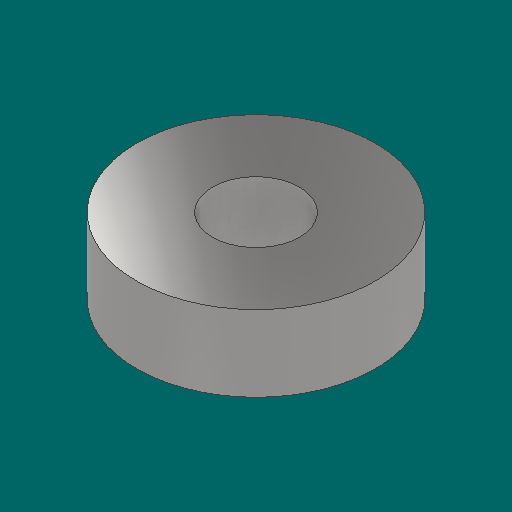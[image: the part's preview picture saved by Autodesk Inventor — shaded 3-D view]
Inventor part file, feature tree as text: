
AUTODESK INVENTOR PART (.ipt)
format: ipt  version: 2023.1 (Build 271208000, 208)  size: 107,008 bytes
history: native  units: in
note: dims shown in document units (in); Inventor stores cm internally (conversion verified against a paired STEP export)
features: other x3, sketch x1
ambient origin geometry x8: Origin, YZ Plane, XZ Plane, XY Plane, X Axis, Y Axis, Z Axis, Center Point
bodies: Solid1 (feature_tree)
feature tree (4):
  other  "608bearing.ipt"
  other  "Solid1::608bearing.ipt"
  other  "TaggingFeature1"
  sketch  "Sketch1"  dims[d0=0.3937in]
